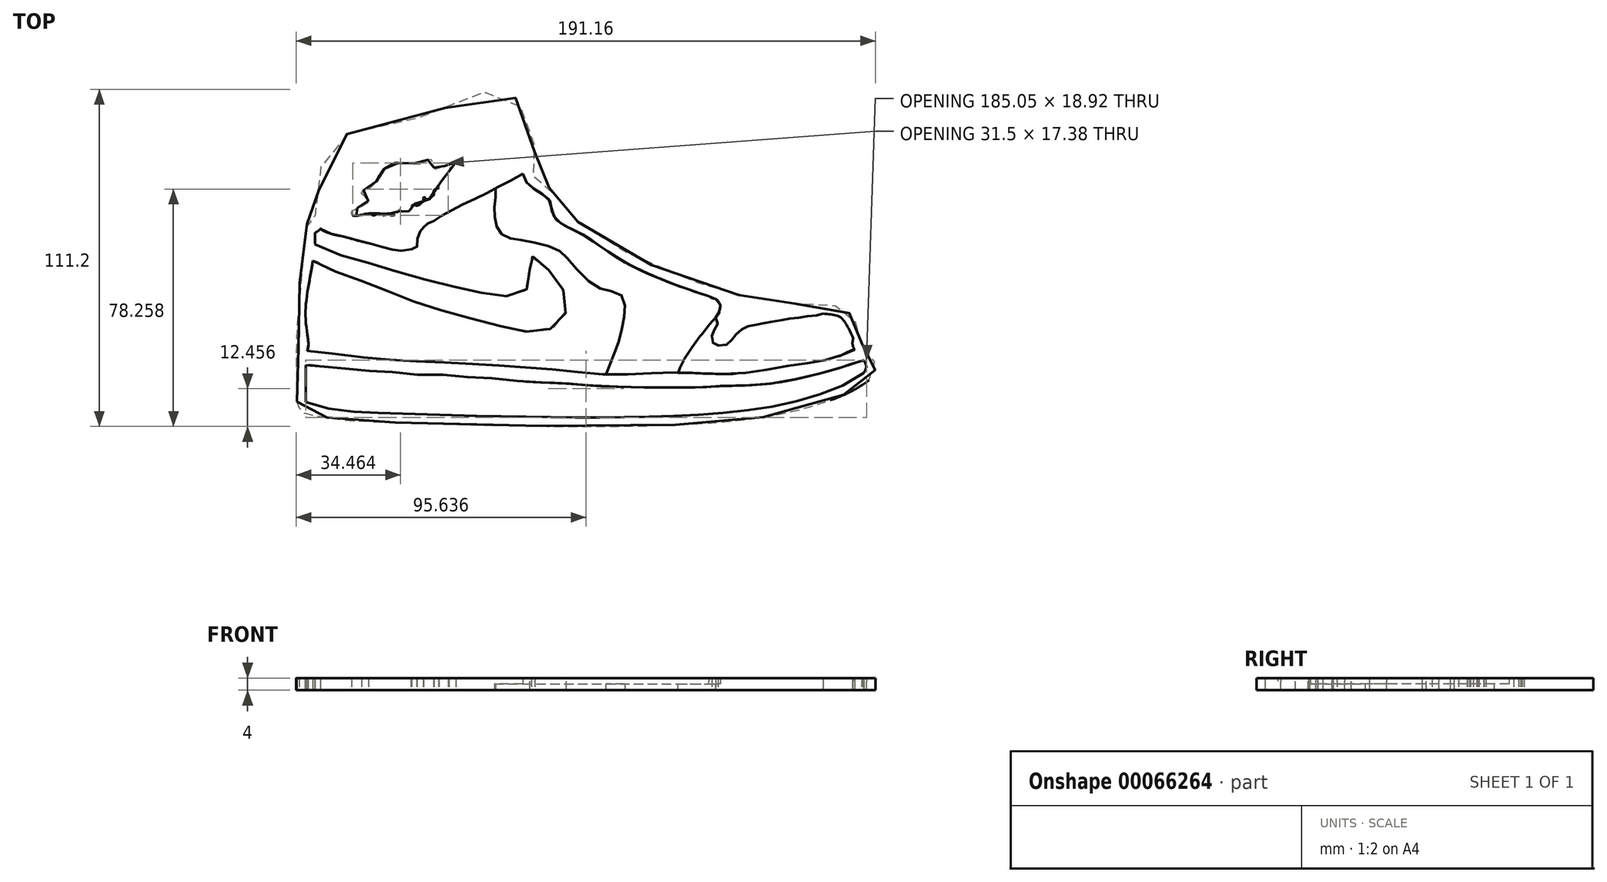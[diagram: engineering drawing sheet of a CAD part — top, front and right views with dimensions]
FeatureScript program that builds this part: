
annotation { "Feature Type Name" : "Feature", "Feature Type Description" : "" }
export const myFeature = defineFeature(function(context is Context, id is Id, definition is map)
    precondition{}
    {
        {
            var Q0;
            Q0=qCreatedBy(makeId("Top.planeOp"),FACE);
            var sketch = newSketch(context, id + "F0", { "sketchPlane" : qUnion([Q0])});
            skFitSpline(sketch, "E0", {"points": [v(-105.9, -66.78) * mm, v(-105.4, -68.5) * mm, v(-103.92, -70.3) * mm, v(-100.83, -71.23) * mm, v(-91.61, -72.73) * mm, v(-84.5, -73.26) * mm, v(-39.64, -74.65) * mm, v(14.68, -74.65) * mm, v(39.9, -73) * mm, v(56.64, -70.3) * mm, v(75.48, -64.16) * mm, v(82.66, -59.97) * mm, v(83.75, -58.87) * mm, v(84.65, -56.98) * mm, v(85.05, -54.99) * mm, v(83.25, -50.5) * mm, v(82.06, -48.9) * mm, v(80.56, -47.91) * mm, v(80.66, -45.92) * mm, v(79.77, -43.13) * mm, v(78.07, -39.94) * mm, v(76.38, -37.55) * mm, v(73.39, -35.66) * mm, v(60.63, -34.46) * mm, v(52.96, -34.06) * mm, v(43.5, -32.47) * mm, v(32.93, -29.78) * mm, v(4.57, -18.6) * mm, v(-10.84, -8.72) * mm, v(-18.55, -4.15) * mm, v(-19.27, 0) * mm, v(-24.08, 4.76) * mm, v(-28.18, 8.13) * mm, v(-27.94, 12.95) * mm, v(-27.46, 18.49) * mm, v(-30.34, 26.67) * mm, v(-36.12, 35.58) * mm, v(-49.37, 33.18) * mm, v(-78.74, 23.06) * mm, v(-95.12, 18.97) * mm, v(-98.25, 6.69) * mm, v(-99.89, -5.37) * mm, v(-100.33, -7.45) * mm, v(-100.78, -8.2) * mm, v(-102.57, -8.35) * mm, v(-102.86, -11.77) * mm, v(-104.23, -23.87) * mm, v(-105.98, -39.83) * mm, v(-105.2, -48.98) * mm, v(-105.88, -49.66) * mm, v(-106, -52.84) * mm, v(-105.9, -66.78) * mm]});
            skSolve(sketch);
        }
        {
            var Q0;
            Q0 = qSketchRegion(id + "F0", true);
            extrude(context, id + "F1", {"entities" : qUnion([Q0]), "depth" : 4 * mm});
        }
        {
            var Q0;
            Q0=makeQuery(id+"F1.opExtrude","CAP_FACE",FACE,{"disambiguationData":[OSD([sQuery(id+"F0.wireOp",EDGE,"E0")])],"isStart":false});
            shell(context, id + "F2", {"entities" : qUnion([Q0]), "thickness" : 3 * mm});
        }
        {
            var Q0;
            {var subQ0=sQuery(id+"F0.wireOp",EDGE,"E0");Q0=makeQuery(id+"F2.opShell","OFFSET_FACE",FACE,{"disambiguationData":[OSD([subQ0]),TDD([makeQuery(id+"F1.opExtrude","CAP_FACE",FACE,{"disambiguationData":[OSD([subQ0])],"isStart":true})])]});}
            extrude(context, id + "F3", {"entities" : qUnion([Q0]), "operationType" : NewBodyOperationType.REMOVE, "oppositeDirection" : true, "depth" : 25 * mm});
        }
        {
            var Q0;
            Q0=qCreatedBy(makeId("Top.planeOp"),FACE);
            var sketch = newSketch(context, id + "F4", { "sketchPlane" : qUnion([Q0])});
            skFitSpline(sketch, "E1", {"points": [v(-100.72, -14.6) * mm, v(-94.94, -17.28) * mm, v(-89.59, -18.95) * mm, v(-82.89, -20.88) * mm, v(-76.03, -22.97) * mm, v(-68.24, -25.32) * mm, v(-60.04, -27.5) * mm, v(-52.34, -29.25) * mm, v(-46.4, -30.6) * mm, v(-40.83, -31.66) * mm, v(-35.5, -31.99) * mm, v(-31.38, -30.9) * mm, v(-29.2, -28.3) * mm, v(-28.99, -24.5) * mm, v(-28.99, -20.48) * mm, v(-28.99, -19.5) * mm, v(-28.23, -18.96) * mm, v(-27.25, -19.6) * mm, v(-23.56, -22.76) * mm, v(-20.2, -26.23) * mm, v(-17.48, -31.45) * mm, v(-17.04, -36.23) * mm, v(-18.13, -39.92) * mm, v(-22.25, -42.85) * mm, v(-27.14, -43.61) * mm, v(-32.25, -43.5) * mm, v(-38.22, -41.98) * mm, v(-46.7, -39.92) * mm, v(-55.38, -37.42) * mm, v(-61.68, -35.8) * mm, v(-68.41, -33.4) * mm, v(-75.26, -30.69) * mm, v(-81.01, -28.3) * mm, v(-88.18, -25.7) * mm, v(-93.72, -23.63) * mm, v(-98.83, -21.02) * mm, v(-101.65, -19.4) * mm, v(-100.84, -15.03) * mm, v(-100.72, -14.6) * mm]});
            skSolve(sketch);
        }
        {
            var Q0;
            Q0 = qSketchRegion(id + "F4", true);
            extrude(context, id + "F5", {"entities" : qUnion([Q0]), "operationType" : NewBodyOperationType.ADD, "depth" : 4 * mm});
        }
        {
            var Q0;
            Q0=qCreatedBy(makeId("Top.planeOp"),FACE);
            var sketch = newSketch(context, id + "F6", { "sketchPlane" : qUnion([Q0])});
            skFitSpline(sketch, "E2", {"points": [v(-103.26, -50.23) * mm, v(-87.7, -51.8) * mm, v(-70.3, -53.26) * mm, v(-51.45, -54.22) * mm, v(-34.29, -55.19) * mm, v(-17.37, -56.64) * mm, v(-2.38, -57.85) * mm, v(11.64, -57.36) * mm, v(24.45, -57.36) * mm, v(38.71, -57.6) * mm, v(49.59, -56.16) * mm, v(59.98, -54.46) * mm, v(67.96, -53.26) * mm, v(74.73, -51.08) * mm, v(78.8, -49.76) * mm, v(81.94, -52.26) * mm, v(77.08, -54.36) * mm, v(72.39, -55.98) * mm, v(65.1, -57.93) * mm, v(57.49, -59.7) * mm, v(50.52, -60.84) * mm, v(42.75, -61.49) * mm, v(34.33, -61.65) * mm, v(27.69, -62.14) * mm, v(19.91, -62.14) * mm, v(12.46, -62.14) * mm, v(4.04, -61.97) * mm, v(-3.4, -61.81) * mm, v(-11.56, -61.27) * mm, v(-19.94, -60.66) * mm, v(-26.69, -60.45) * mm, v(-34.25, -59.84) * mm, v(-41.81, -59.02) * mm, v(-48.97, -58.82) * mm, v(-56.12, -58) * mm, v(-63.9, -58) * mm, v(-71.66, -57.39) * mm, v(-78.4, -56.77) * mm, v(-84.75, -56.57) * mm, v(-91.48, -55.76) * mm, v(-96.82, -55.29) * mm, v(-101.31, -54.63) * mm, v(-103.65, -54.45) * mm, v(-103.6, -51.19) * mm, v(-103.26, -50.23) * mm]});
            skSolve(sketch);
        }
        {
            var Q0;
            Q0 = qSketchRegion(id + "F6", true);
            extrude(context, id + "F7", {"entities" : qUnion([Q0]), "operationType" : NewBodyOperationType.ADD, "depth" : 4 * mm});
        }
        {
            var Q0;
            Q0=qCreatedBy(makeId("Top.planeOp"),FACE);
            var sketch = newSketch(context, id + "F8", { "sketchPlane" : qUnion([Q0])});
            skFitSpline(sketch, "E3", {"points": [v(29.19, -30.84) * mm, v(30.43, -32.32) * mm, v(32.15, -32.94) * mm, v(33.4, -34.03) * mm, v(33.86, -35.27) * mm, v(33.63, -36.6) * mm, v(32.93, -38.47) * mm, v(32.3, -39.01) * mm, v(33.08, -39.95) * mm, v(32.54, -41.97) * mm, v(31.91, -43.06) * mm, v(31.37, -44.15) * mm, v(31.06, -45.24) * mm, v(31.21, -47.03) * mm, v(31.76, -47.74) * mm, v(32.85, -48.2) * mm, v(34.8, -48.36) * mm, v(36.5, -47.66) * mm, v(37.52, -46.49) * mm, v(38.38, -45.48) * mm, v(39.4, -44.23) * mm, v(40.8, -43.06) * mm, v(41.96, -42.05) * mm, v(43.83, -41.9) * mm, v(46.09, -41.35) * mm, v(47.65, -41.04) * mm, v(49.67, -40.73) * mm, v(52.24, -40.26) * mm, v(54.73, -39.8) * mm, v(56.68, -39.48) * mm, v(58.86, -39.17) * mm, v(61.12, -38.94) * mm, v(63.77, -38.47) * mm, v(65.87, -38.31) * mm, v(66.8, -38) * mm, v(68.36, -37.61) * mm, v(40.8, -34.03) * mm, v(32.46, -31.77) * mm, v(30.36, -31.15) * mm, v(29.19, -30.84) * mm]});
            skSolve(sketch);
        }
        {
            var Q0;
            Q0 = qSketchRegion(id + "F8", true);
            extrude(context, id + "F9", {"entities" : qUnion([Q0]), "operationType" : NewBodyOperationType.ADD, "depth" : 4 * mm});
        }
        {
            var Q0;
            Q0=qCreatedBy(makeId("Top.planeOp"),FACE);
            var sketch = newSketch(context, id + "F10", { "sketchPlane" : qUnion([Q0])});
            skFitSpline(sketch, "E4", {"points": [v(-30.15, 9.47) * mm, v(-36.83, 5.32) * mm, v(-43.7, 1.7) * mm, v(-51.63, -2.08) * mm, v(-57.4, -5.15) * mm, v(-61.2, -7.5) * mm, v(-62.64, -8.04) * mm, v(-63.73, -8.94) * mm, v(-64.8, -10.2) * mm, v(-65.71, -11.47) * mm, v(-66.25, -15.26) * mm, v(-66.25, -15.9) * mm, v(-69.98, -16.95) * mm, v(-73.93, -16.8) * mm, v(-79.16, -15.4) * mm, v(-84.67, -13.98) * mm, v(-90.33, -12.42) * mm, v(-93.58, -11.72) * mm, v(-98.8, -8.9) * mm, v(-97.39, -1.8) * mm, v(-96.6, 6.72) * mm, v(-95.92, 12.4) * mm, v(-94.25, 17.68) * mm, v(-85.83, 19.84) * mm, v(-70.8, 23.35) * mm, v(-57.63, 28.18) * mm, v(-47.53, 32.13) * mm, v(-40.5, 34.32) * mm, v(-38.02, 34.9) * mm, v(-35.24, 32.57) * mm, v(-29.68, 21.3) * mm, v(-29.1, 16.76) * mm, v(-29.82, 12.08) * mm, v(-30.15, 9.47) * mm]});
            skSolve(sketch);
        }
        {
            var Q0;
            Q0 = qSketchRegion(id + "F10", true);
            extrude(context, id + "F11", {"entities" : qUnion([Q0]), "operationType" : NewBodyOperationType.ADD, "depth" : 4 * mm});
        }
        {
            var Q0;
            Q0=qCreatedBy(makeId("Top.planeOp"),FACE);
            var sketch = newSketch(context, id + "F12", { "sketchPlane" : qUnion([Q0])});
            skFitSpline(sketch, "E5", {"points": [v(-72.5, 11.96) * mm, v(-70.82, 12.16) * mm, v(-70.06, 12.11) * mm, v(-69.05, 12.01) * mm, v(-67.88, 11.8) * mm, v(-66.76, 11.7) * mm, v(-65.95, 11.55) * mm, v(-65.09, 11.66) * mm, v(-64.07, 12.06) * mm, v(-63.16, 12.57) * mm, v(-62.55, 12.98) * mm, v(-62.14, 13.23) * mm, v(-61.68, 13.28) * mm, v(-61.38, 12.42) * mm, v(-61.07, 11.7) * mm, v(-60.87, 10.94) * mm, v(-60.62, 10.49) * mm, v(-60.72, 10.08) * mm, v(-60.57, 9.83) * mm, v(-59.8, 9.98) * mm, v(-59, 10.18) * mm, v(-58.28, 10.64) * mm, v(-57.42, 10.84) * mm, v(-56.45, 11.3) * mm, v(-55.7, 11.76) * mm, v(-54.88, 12.26) * mm, v(-54.17, 12.42) * mm, v(-53.36, 12.57) * mm, v(-53.76, 11.7) * mm, v(-54.47, 10.94) * mm, v(-54.98, 10.34) * mm, v(-55.44, 9.98) * mm, v(-55.9, 9.67) * mm, v(-55.64, 9.32) * mm, v(-56.2, 8.66) * mm, v(-56.66, 8.05) * mm, v(-57.11, 7.6) * mm, v(-57.52, 7.19) * mm, v(-57.98, 6.32) * mm, v(-58.13, 5.92) * mm, v(-58.69, 5.4) * mm, v(-59.04, 4.95) * mm, v(-59, 4.5) * mm, v(-59, 4.09) * mm, v(-59, 3.73) * mm, v(-59.25, 3.53) * mm, v(-59.6, 3.43) * mm, v(-59.9, 3.28) * mm, v(-60.46, 3.07) * mm, v(-60.77, 2.26) * mm, v(-60.62, 1.75) * mm, v(-60.77, 1.2) * mm, v(-61.33, 0.79) * mm, v(-62.14, 0) * mm, v(-62.24, 0) * mm, v(-63, 0) * mm, v(-63.51, 0) * mm, v(-63.77, 0.59) * mm, v(-64.02, 0.64) * mm, v(-64.22, 0) * mm, v(-64.07, -0.48) * mm, v(-64.07, -0.79) * mm, v(-64.88, -1.4) * mm, v(-65.24, -1.75) * mm, v(-65.75, -2.06) * mm, v(-66.25, -2.2) * mm, v(-66.66, -2.26) * mm, v(-67.02, -1.6) * mm, v(-67.37, -1.95) * mm, v(-67.83, -2.06) * mm, v(-68.08, -2.06) * mm, v(-68.28, -2.26) * mm, v(-67.98, -2.92) * mm, v(-68.28, -3.48) * mm, v(-68.84, -3.88) * mm, v(-69.45, -4.19) * mm, v(-71.08, -4.29) * mm, v(-71.48, -3.78) * mm, v(-71.79, -3.43) * mm, v(-72.1, -3.48) * mm, v(-72.4, -3.99) * mm, v(-72.55, -4.5) * mm, v(-73.31, -5.05) * mm, v(-74.18, -5.36) * mm, v(-74.53, -5.36) * mm, v(-74.68, -5.4) * mm, v(-75.24, -5.2) * mm, v(-75.34, -4.95) * mm, v(-75.75, -4.7) * mm, v(-76.16, -5.1) * mm, v(-76.82, -5.2) * mm, v(-77.43, -5.4) * mm, v(-77.58, -5.46) * mm, v(-77.93, -5.05) * mm, v(-78.24, -4.8) * mm, v(-78.6, -4.7) * mm, v(-79.05, -4.85) * mm, v(-79.6, -5.1) * mm, v(-79.96, -5.25) * mm, v(-80.32, -5.36) * mm, v(-81.18, -5.15) * mm, v(-81.49, -4.85) * mm, v(-81.7, -4.7) * mm, v(-82.4, -4.8) * mm, v(-83.21, -4.9) * mm, v(-83.82, -5.05) * mm, v(-84.59, -5.25) * mm, v(-85.96, -5.46) * mm, v(-86.46, -5.46) * mm, v(-87.43, -5.4) * mm, v(-87.73, -5) * mm, v(-87.79, -3.93) * mm, v(-86.82, -3.43) * mm, v(-85.65, -2.87) * mm, v(-84.94, -2.61) * mm, v(-83.82, -2) * mm, v(-83.27, -1.65) * mm, v(-82.66, -1.3) * mm, v(-82.25, -0.74) * mm, v(-82.66, 0) * mm, v(-83.42, 0.89) * mm, v(-83.77, 1.2) * mm, v(-84.13, 1.6) * mm, v(-84.54, 2.26) * mm, v(-83.98, 2.82) * mm, v(-82.8, 3.23) * mm, v(-82.15, 3.58) * mm, v(-81.08, 4.2) * mm, v(-80.37, 5) * mm, v(-79.5, 5.97) * mm, v(-79.15, 6.73) * mm, v(-78.6, 7.8) * mm, v(-78.04, 8.6) * mm, v(-77.53, 9.32) * mm, v(-76.87, 10.03) * mm, v(-75.9, 10.64) * mm, v(-74.89, 11.25) * mm, v(-73.87, 11.7) * mm, v(-73.31, 11.9) * mm, v(-72.5, 11.96) * mm]});
            skSolve(sketch);
        }
        {
            var Q0;
            Q0 = qSketchRegion(id + "F12", true);
            extrude(context, id + "F13", {"entities" : qUnion([Q0]), "operationType" : NewBodyOperationType.REMOVE, "depth" : 4 * mm});
        }
        {
            var Q0;
            Q0=makeQuery(id+"F11.boolean.opBoolean","MERGE",FACE,{"derivedFrom":[makeQuery(id+"F9.boolean.opBoolean","MERGE",FACE,{"derivedFrom":[makeQuery(id+"F7.boolean.opBoolean","MERGE",FACE,{"derivedFrom":[makeQuery(id+"F5.boolean.opBoolean","MERGE",FACE,{"derivedFrom":[makeQuery(id+"F1.opExtrude","CAP_FACE",FACE,{"disambiguationData":[OSD([sQuery(id+"F0.wireOp",EDGE,"E0")])],"isStart":false}),makeQuery(id+"F5.opExtrude","CAP_FACE",FACE,{"disambiguationData":[OSD([sQuery(id+"F4.wireOp",EDGE,"E1")])],"isStart":false})]}),makeQuery(id+"F7.opExtrude","CAP_FACE",FACE,{"disambiguationData":[OSD([sQuery(id+"F6.wireOp",EDGE,"E2")])],"isStart":false})]}),makeQuery(id+"F9.opExtrude","CAP_FACE",FACE,{"disambiguationData":[OSD([sQuery(id+"F8.wireOp",EDGE,"E3")])],"isStart":false})]}),makeQuery(id+"F11.opExtrude","CAP_FACE",FACE,{"disambiguationData":[OSD([sQuery(id+"F10.wireOp",EDGE,"E4")])],"isStart":false})]});
            var sketch = newSketch(context, id + "F14", { "sketchPlane" : qUnion([Q0])});
            skFitSpline(sketch, "E6", {"points": [v(-40.35, 3.47) * mm, v(-40.3, 0.58) * mm, v(-40.7, -3.49) * mm, v(-40.37, -7.05) * mm, v(-39.34, -10.54) * mm, v(-36.36, -12.67) * mm, v(-32.42, -13.47) * mm, v(-25, -14.9) * mm, v(-19.06, -17.19) * mm, v(-15.74, -20.5) * mm, v(-8.56, -27.91) * mm, v(-3.18, -30.24) * mm, v(1.33, -31.78) * mm, v(2.33, -36.5) * mm, v(1.57, -41.56) * mm, v(0, -48) * mm, v(-1.97, -52.88) * mm, v(-3.9, -57.8) * mm], "startDerivative": vector(6.1, -60.86) * mm, "endDerivative": vector(-32.2, -82.65) * mm});
            skFitSpline(sketch, "E7", {"points": [v(19.91, -57.26) * mm, v(21.7, -53.32) * mm, v(24.4, -49.09) * mm, v(28.5, -43.57) * mm, v(32.3, -38.99) * mm], "startDerivative": vector(7.26, 18.85) * mm, "endDerivative": vector(14.5, 17) * mm});
            skSolve(sketch);
        }
        {
            var Q0;
            {var subQ14=sQuery(id+"F14.wireOp",EDGE,"E6");Q0=makeQuery(id+"F14.imprint","IMPRINT",FACE,{"disambiguationData":[TD([[makeQuery(id+"F14.imprint","IMPRINT",EDGE,{"derivedFrom":subQ14}),1.0]])]});}
            extrude(context, id + "F15", {"entities" : qUnion([Q0]), "operationType" : NewBodyOperationType.ADD, "oppositeDirection" : true, "depth" : 4 * mm, "hasSecondDirection" : true, "secondDirectionOppositeDirection" : true, "secondDirectionDepth" : 2 * mm});
        }
    });
